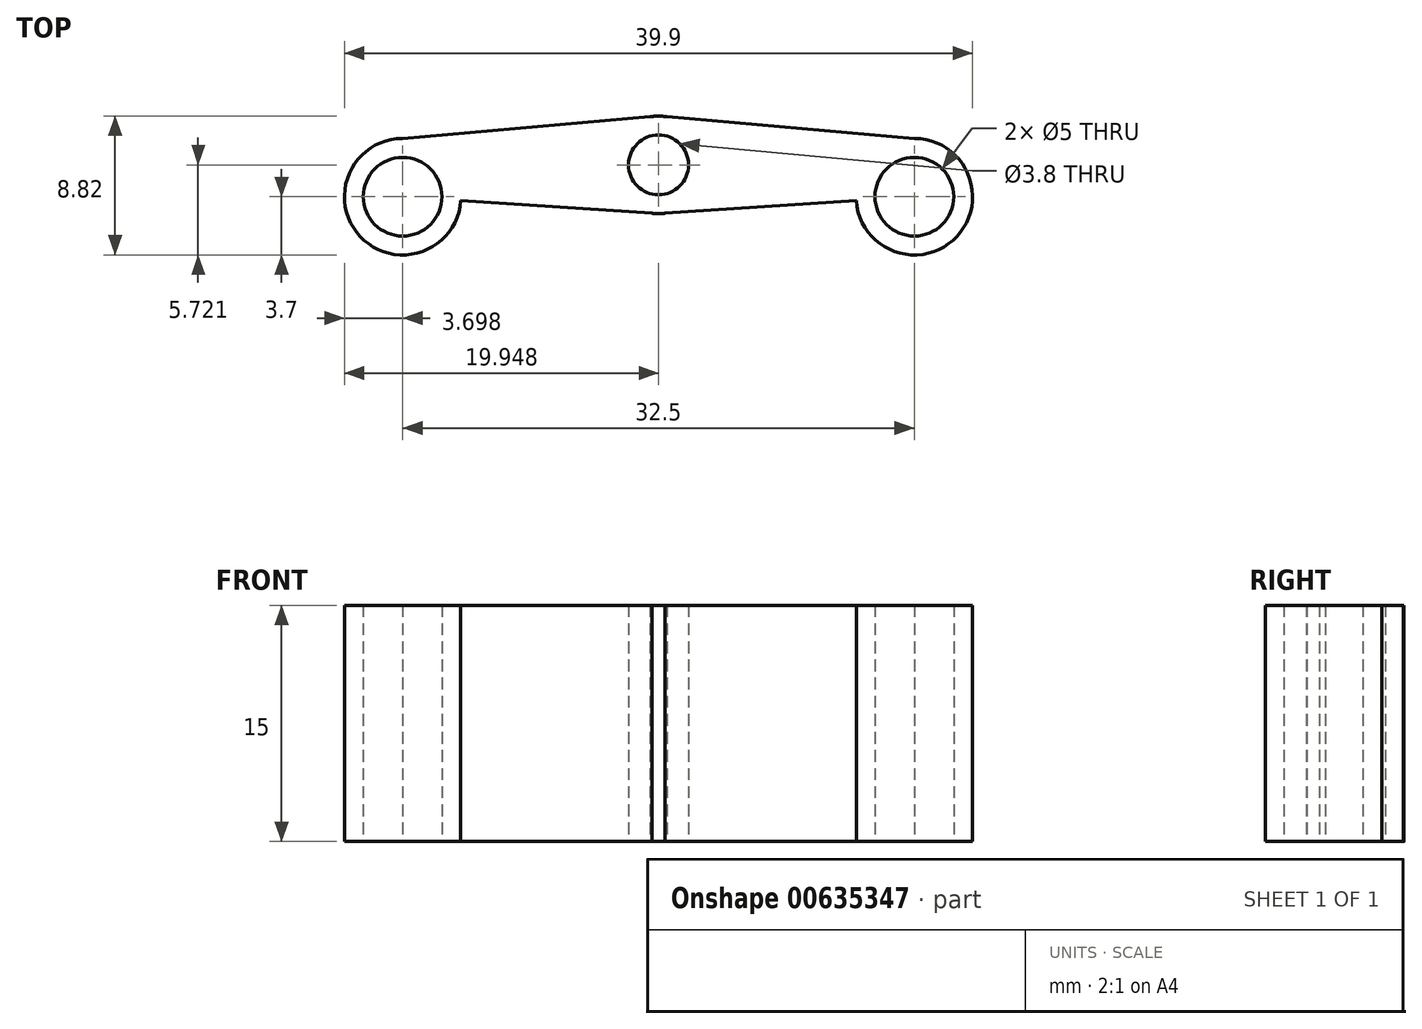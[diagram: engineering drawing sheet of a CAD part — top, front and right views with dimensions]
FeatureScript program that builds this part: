
annotation { "Feature Type Name" : "Feature", "Feature Type Description" : "" }
export const myFeature = defineFeature(function(context is Context, id is Id, definition is map)
    precondition{}
    {
        {
            var Q0;
            Q0=qCreatedBy(makeId("Top.planeOp"),FACE);
            var sketch = newSketch(context, id + "F0", { "sketchPlane" : qUnion([Q0])});
            skCircle(sketch, "E0", {"center": v(-10.82, 2.02) * mm, "radius": 1.9 * mm});
            skCircle(sketch, "E1", {"center": v(-27.07, 0) * mm, "radius": 2.5 * mm});
            skCircle(sketch, "E2", {"center": v(5.43, 0) * mm, "radius": 2.5 * mm});
            skLineSegment(sketch, "E3", {"start": v(-24.6, 0.3) * mm, "end": v(-12.7, 1.79) * mm});
            skLineSegment(sketch, "E4", {"start": v(2.95, 0.3) * mm, "end": v(-8.94, 1.79) * mm});
            skCircle(sketch, "E5", {"center": v(-27.07, 0) * mm, "radius": 3.7 * mm});
            skCircle(sketch, "E6", {"center": v(5.43, 0) * mm, "radius": 3.7 * mm});
            skCircle(sketch, "E7", {"center": v(-10.82, 2.02) * mm, "radius": 3.1 * mm});
            skLineSegment(sketch, "E8", {"start": v(-27.07, 2.5) * mm, "end": v(-27.07, 3.7) * mm});
            skLineSegment(sketch, "E9", {"start": v(-27.07, 3.7) * mm, "end": v(-10.82, 5.12) * mm});
            skLineSegment(sketch, "E10", {"start": v(-10.82, 5.12) * mm, "end": v(5.43, 3.7) * mm});
            skLineSegment(sketch, "E11", {"start": v(5.43, 3.7) * mm, "end": v(5.43, 2.5) * mm});
            skLineSegment(sketch, "E12", {"start": v(2.93, -0.17) * mm, "end": v(-10.82, -1.08) * mm});
            skLineSegment(sketch, "E13", {"start": v(-10.82, -1.08) * mm, "end": v(-24.58, -0.17) * mm});
            skSolve(sketch);
        }
        {
            var Q0;
            Q0 = qSketchRegion(id + "F0", true);
            extrude(context, id + "F1", {"entities" : qUnion([Q0]), "depth" : 15 * mm, "offsetDistance" : 25 * mm});
        }
    });
